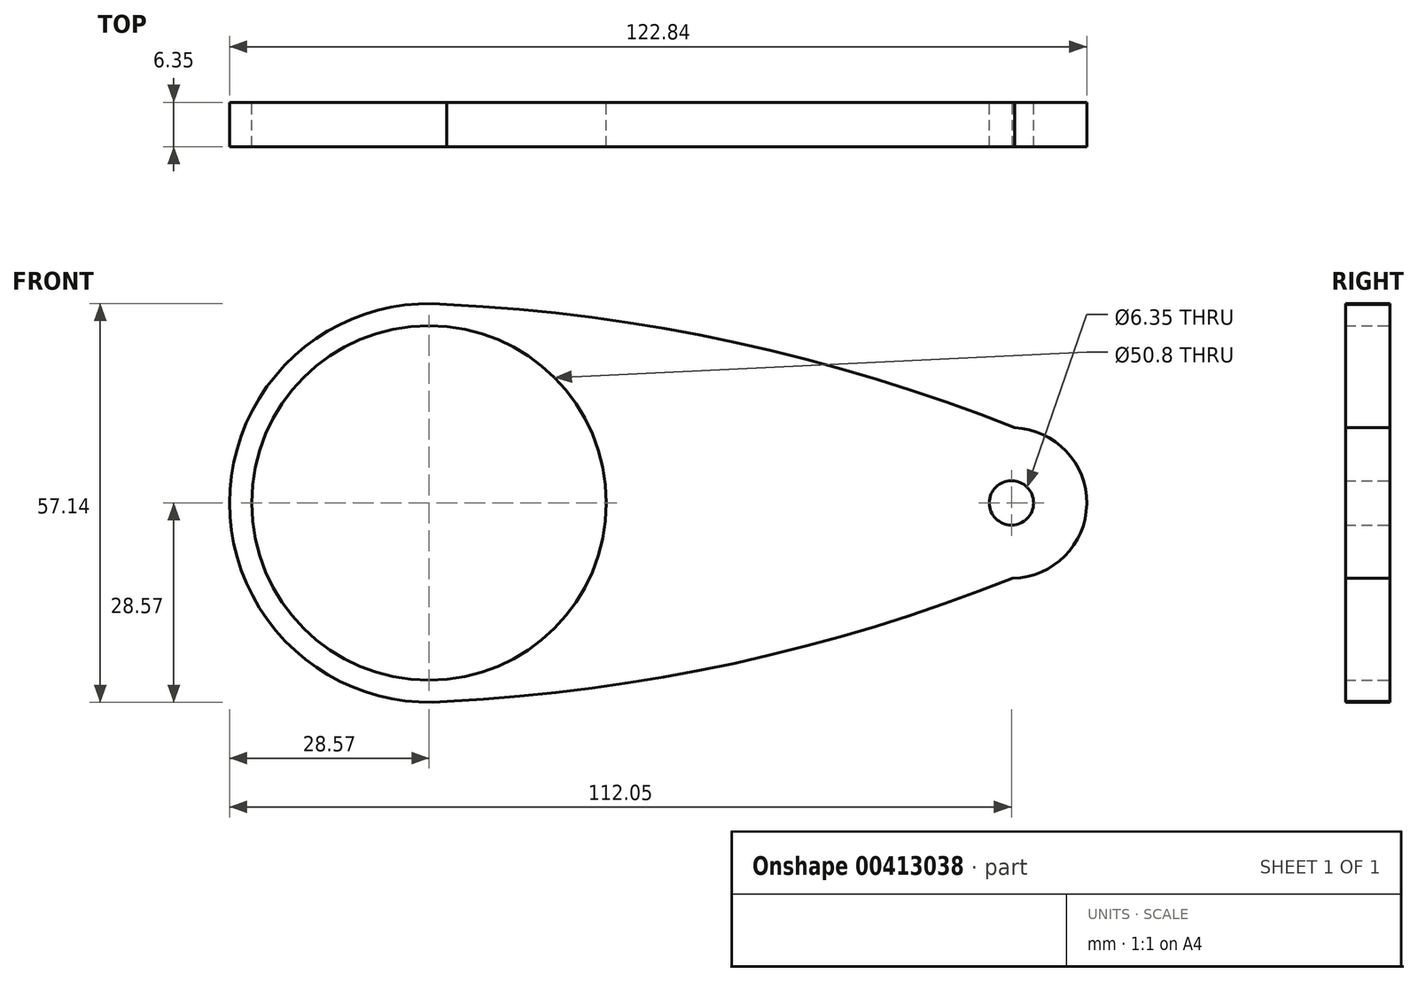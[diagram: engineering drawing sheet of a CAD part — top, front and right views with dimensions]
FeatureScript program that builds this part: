
annotation { "Feature Type Name" : "Feature", "Feature Type Description" : "" }
export const myFeature = defineFeature(function(context is Context, id is Id, definition is map)
    precondition{}
    {
        {
            var Q0;
            Q0=qCreatedBy(makeId("Front.planeOp"),FACE);
            var sketch = newSketch(context, id + "F0", { "sketchPlane" : qUnion([Q0])});
            skCircle(sketch, "E0", {"center": v(0, 0) * mm, "radius": 25.4 * mm});
            skCircle(sketch, "E1", {"center": v(0, 0) * mm, "radius": 28.58 * mm});
            skCircle(sketch, "E2", {"center": v(83.48, 0) * mm, "radius": 10.8 * mm});
            skArc(sketch, "E3", {"start": v(83.94, 10.79) * mm, "mid": v(42.72, 23.25) * mm, "end": v(0, 28.58) * mm});
            skArc(sketch, "E4", {"start": v(0, -28.57) * mm, "mid": v(42.59, -23.23) * mm, "end": v(83.67, -10.8) * mm});
            skCircle(sketch, "E5", {"center": v(83.48, 0) * mm, "radius": 3.18 * mm});
            skSolve(sketch);
        }
        {
            var Q0;
            Q0 = qSketchRegion(id + "F0", true);
            extrude(context, id + "F1", {"entities" : qUnion([Q0]), "depth" : 6.35 * mm});
        }
    });
